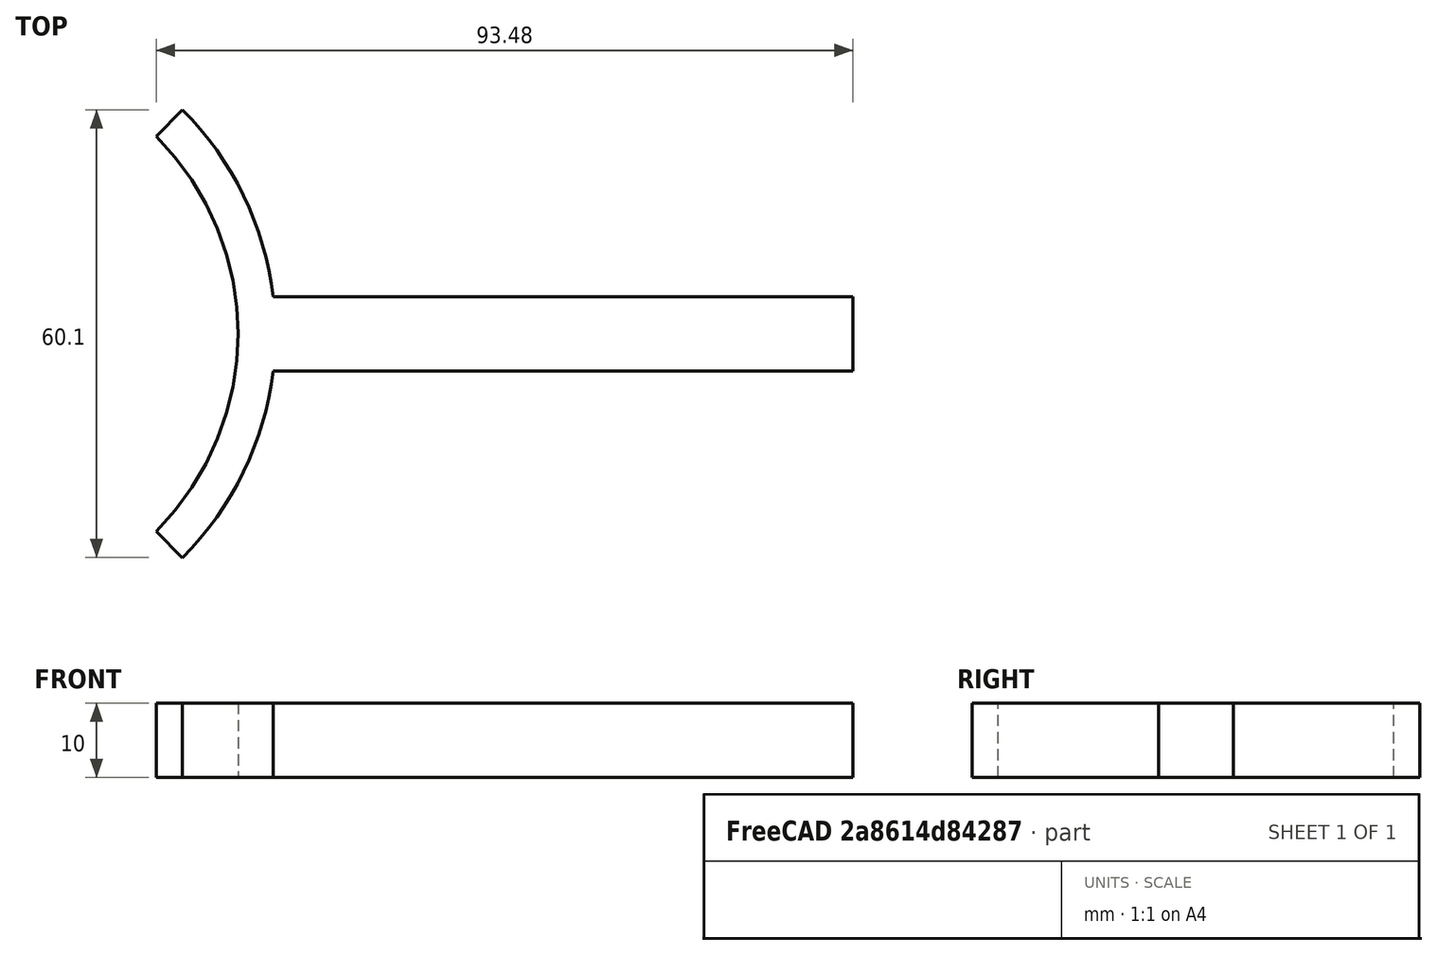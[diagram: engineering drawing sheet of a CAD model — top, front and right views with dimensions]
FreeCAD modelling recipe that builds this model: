
FCSTD DOCUMENT  (FreeCAD 0.19R24276 (Git))
Label: vilka_75x120
License: All rights reserved
LicenseURL: http://en.wikipedia.org/wiki/All_rights_reserved
objects: Sketcher::SketchObject×2, PartDesign::Pad×1, PartDesign::Body×1
note: 5 computed .brp shape members not serialized (recipe doc carries the construction recipe); baked Part::Feature solids carry a one-line shape summary decoded from their .brp

FEATURE [Sketcher::SketchObject] Sketch
  FullyConstrained = true
  MapMode = 5
  Support = -> [XY_Plane]
FEATURE [Sketcher::SketchObject] Sketch001
  FullyConstrained = false
  MapMode = 5
  Support = -> [XY_Plane]
  sketch-geometry (8):
    g0: ArcOfCircle CenterX=0 CenterY=0 CenterZ=0 NormalX=0 NormalY=0 NormalZ=1 AngleXU=0 Radius=37.5 StartAngle=5.49779 EndAngle=7.06858
    g1: ArcOfCircle CenterX=0 CenterY=0 CenterZ=0 NormalX=0 NormalY=0 NormalZ=1 AngleXU=0 Radius=42.5 StartAngle=0.11792 EndAngle=0.785398
    g2: LineSegment StartX=26.5165 StartY=26.5165 StartZ=0 EndX=30.052 EndY=30.052 EndZ=0
    g3: LineSegment StartX=26.5165 StartY=-26.5165 StartZ=0 EndX=30.052 EndY=-30.052 EndZ=0
    g4: LineSegment StartX=42.2049 StartY=5 StartZ=0 EndX=120 EndY=5 EndZ=0
    g5: LineSegment StartX=42.2049 StartY=-5 StartZ=0 EndX=120 EndY=-5 EndZ=0
    g6: LineSegment StartX=120 StartY=5 StartZ=0 EndX=120 EndY=-5 EndZ=0
    g7: ArcOfCircle CenterX=0 CenterY=0 CenterZ=0 NormalX=0 NormalY=0 NormalZ=1 AngleXU=0 Radius=42.5 StartAngle=5.49779 EndAngle=6.16527
  constraints (17):
    c: Coincident(g0,g-1)
    c: Diameter(g0) = 75
    c: Diameter(g1) = 85
    c: Coincident(g1,g0)
    c: Horizontal(g4)
    c: Horizontal(g5)
    c: Vertical(g6)
    c: Coincident(g6,g5)
    c: Coincident(g6,g4)
    c: Coincident(g7,g5)
    c: Coincident(g1,g4)
    c: Equal(g1,g7)
    c: Coincident(g1,g7)
    c: Coincident(g2,g0)
    c: Coincident(g3,g0)
    c: Coincident(g3,g7)
    c: Coincident(g2,g1)
FEATURE [PartDesign::Pad] Pad
  Direction = (1,1,1)
  Length = 10
  Length2 = 100
  Profile = -> Sketch001
  Type = 0
FEATURE [PartDesign::Body] Body
  Group = -> [Sketch,Sketch001,Pad]
  Origin = -> Origin
  Tip = -> Pad
